AUTODESK INVENTOR PART (.ipt)
format: ipt  version: 2022 (Build 260153070, 153G)  size: 187,392 bytes
history: native  units: in
note: dims shown in document units (in); Inventor stores cm internally (conversion verified against a paired STEP export)
features: sketch x13, extrude x7, fillet x1
ambient origin geometry x8: Origin, YZ Plane, XZ Plane, XY Plane, X Axis, Y Axis, Z Axis, Center Point
bodies: Solid1 (feature_tree)
feature tree (21):
  sketch  "Sketch1"  dims[d0=4.5in d1=4.5in]
  extrude  "Extrusion1"  Depth=4.5in
  extrude  "Extrusion2"  Depth=0.157in
  extrude  "Extrusion3"  Depth=0.157in
  extrude  "Extrusion4"  Depth=4.343in TaperAngle=0.0deg
  fillet  "Fillet3"  Radius=0.394in
  sketch  "Sketch7"  dims[d22=2.0in d23=2.25in]
  sketch  "Sketch8"  dims[d24=2.25in d25=0.0in d26=0.0in]
  extrude  "Extrusion5"  Depth=2.0in
  sketch  "Sketch9"  dims[d27=0.157in]
  sketch  "Sketch10"  dims[d28=0.157in]
  extrude  "Extrusion6"  Depth=2.25in
  sketch  "Sketch16"  dims[d29=0.157in]
  sketch  "Sketch17"  dims[d30=0.157in]
  extrude  "Extrusion11"  TaperAngle=0.0deg  [1 undecoded]
  sketch  "Sketch19"  dims[d32=2.25in d33=2.25in d34=2.25in d35=2.0in d36=2.0in d37=3.0in d38=3.0in d39=0.0in d40=0.0in d42=0.0787in d43=0.787in d44=0.787in d45=2.5in d46=0.787in d47=1.0in d48=1.0in d49=1.181in d50=1.181in d51=1.181in d52=1.181in d53=0.157in d54=0.0in d55=0.157in d56=0.157in d57=0.157in d58=0.157in d59=0.75in d60=0.75in d61=0.75in d62=0.75in d63=0.75in d64=0.75in d65=0.75in d66=0.75in d67=0.157in d68=0.0in d89=0.157in d90=0.157in d91=1.0in d92=0.5in d93=1.0in d94=0.0in]
  sketch  "Sketch2"  dims[d2=10.0in d3=0.0in d4=0.157in]
  sketch  "Sketch3"  dims[d5=0.157in d6=0.157in]
  sketch  "Sketch5"  dims[d7=0.157in d8=4.343in d9=0.0in d19=0.394in]
  sketch  "Sketch6"  dims[d20=0.394in d21=2.0in]
  sketch  "Sketch18"  dims[d31=2.25in]
note: 1 required parameter value undecoded (feature->parameter linkage not recoverable at this tier; creation-order binding heuristic only, values carry confidence <= 0.55)
